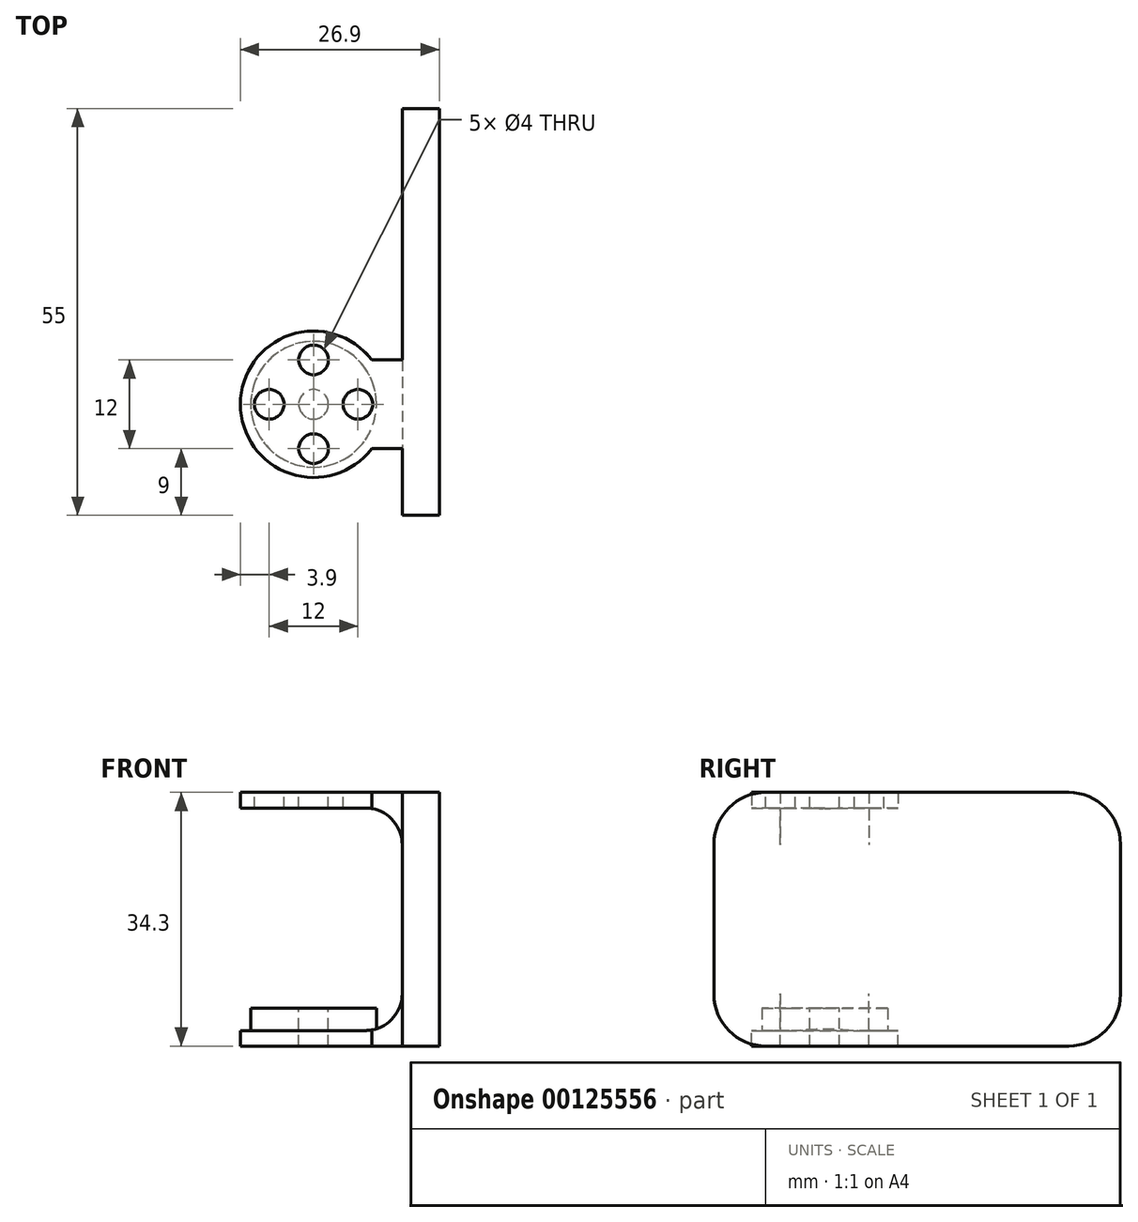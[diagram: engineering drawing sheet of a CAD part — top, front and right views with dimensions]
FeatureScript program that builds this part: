
annotation { "Feature Type Name" : "Feature", "Feature Type Description" : "" }
export const myFeature = defineFeature(function(context is Context, id is Id, definition is map)
    precondition{}
    {
        {
            var Q0;
            Q0=qCreatedBy(makeId("Top.planeOp"),FACE);
            var sketch = newSketch(context, id + "F0", { "sketchPlane" : qUnion([Q0])});
            skArc(sketch, "E0", {"start": v(7.87, 6) * mm, "mid": v(-9.9, 0) * mm, "end": v(7.87, -6) * mm});
            skLineSegment(sketch, "E1", {"start": v(7.87, 6) * mm, "end": v(12, 6) * mm});
            skLineSegment(sketch, "E2", {"start": v(12, 6) * mm, "end": v(12, 40) * mm});
            skLineSegment(sketch, "E3", {"start": v(12, 40) * mm, "end": v(17, 40) * mm});
            skLineSegment(sketch, "E4", {"start": v(17, 40) * mm, "end": v(17, -15) * mm});
            skLineSegment(sketch, "E5", {"start": v(17, -15) * mm, "end": v(12, -15) * mm});
            skLineSegment(sketch, "E6", {"start": v(12, -15) * mm, "end": v(12, -6) * mm});
            skLineSegment(sketch, "E7", {"start": v(12, -6) * mm, "end": v(7.87, -6) * mm});
            skSolve(sketch);
        }
        {
            var Q0;
            Q0=qSketchRegion(id+"F0",true);
            extrude(context, id + "F1", {"entities" : qUnion([Q0]), "depth" : 17.15 * mm});
        }
        {
            var Q0;
            Q0=qCreatedBy(makeId("Front.planeOp"),FACE);
            var sketch = newSketch(context, id + "F2", { "sketchPlane" : qUnion([Q0])});
            skLineSegment(sketch, "E8.bottom", {"start": v(-20, 15.05) * mm, "end": v(7, 15.05) * mm});
            skLineSegment(sketch, "E8.top", {"start": v(-20, 0) * mm, "end": v(12, 0) * mm});
            skLineSegment(sketch, "E8.left", {"start": v(-20, 15.05) * mm, "end": v(-20, 0) * mm});
            skLineSegment(sketch, "E8.right", {"start": v(12, 10.05) * mm, "end": v(12, 0) * mm});
            skPoint(sketch, "E9.visualSharp", {"position": v(12, 15.05) * mm});
            skArc(sketch, "E9.filletArc", {"start": v(12, 10.05) * mm, "mid": v(10.54, 13.59) * mm, "end": v(7, 15.05) * mm});
            skSolve(sketch);
        }
        {
            var Q0;
            Q0=qSketchRegion(id+"F2",true);
            extrude(context, id + "F3", {"entities" : qUnion([Q0]), "operationType" : NewBodyOperationType.REMOVE, "endBound" : BoundingType.THROUGH_ALL, "oppositeDirection" : true, "depth" : 25 * mm, "hasSecondDirection" : true, "secondDirectionBound" : BoundingType.THROUGH_ALL, "secondDirectionOppositeDirection" : false, "secondDirectionDepth" : 25 * mm});
        }
        {
            var Q0;
            Q0=makeQuery(id+"F1.opExtrude","SWEPT_BODY",BODY,{"disambiguationData":[OSD([sQuery(id+"F0.wireOp",EDGE,"E0"),sQuery(id+"F0.wireOp",EDGE,"6P5EcGxq-JUqI-CBL5-0zC6-SwB43NatiXiN"),sQuery(id+"F0.wireOp",EDGE,"WmPqxOhL-y9bk-pV19-5UxV-K0lxU9I4QW50"),sQuery(id+"F0.wireOp",EDGE,"Di974qKV-glCy-LQtE-R6xi-RdLjh6y6jq4b")])]});
            var Q1;
            Q1=qCreatedBy(makeId("Top.planeOp"),FACE);
            mirror(context, id + "F4", {"operationType" : NewBodyOperationType.ADD, "entities" : qUnion([Q0]), "mirrorPlane" : qUnion([Q1])});
        }
        {
            var Q0;
            Q0=makeQuery(id+"F4.opPattern","COPY",FACE,{"derivedFrom":makeQuery(id+"F3.boolean.opBoolean","COPY",FACE,{"derivedFrom":makeQuery(id+"F3.opExtrude","SWEPT_FACE",FACE,{"disambiguationData":[OSD([sQuery(id+"F2.wireOp",EDGE,"E8.bottom")])]})}),"instanceName":"1"});
            var sketch = newSketch(context, id + "F5", { "sketchPlane" : qUnion([Q0])});
            skCircle(sketch, "E10", {"center": v(0, 0) * mm, "radius": 8.5 * mm});
            skSolve(sketch);
        }
        {
            var Q0;
            Q0=qSketchRegion(id+"F5",true);
            extrude(context, id + "F6", {"entities" : qUnion([Q0]), "operationType" : NewBodyOperationType.ADD, "depth" : 3 * mm});
        }
        {
            var Q0;
            Q0=makeQuery(id+"F6.opExtrude","CAP_FACE",FACE,{"disambiguationData":[OSD([sQuery(id+"F5.wireOp",EDGE,"E10")])],"isStart":false});
            var sketch = newSketch(context, id + "F7", { "sketchPlane" : qUnion([Q0])});
            skCircle(sketch, "E11", {"center": v(0, 0) * mm, "radius": 2 * mm});
            skSolve(sketch);
        }
        {
            var Q0;
            Q0=qSketchRegion(id+"F7",true);
            extrude(context, id + "F8", {"entities" : qUnion([Q0]), "operationType" : NewBodyOperationType.REMOVE, "endBound" : BoundingType.THROUGH_ALL, "oppositeDirection" : true, "depth" : 25 * mm});
        }
        {
            var Q0;
            Q0=makeQuery(id+"F1.opExtrude","CAP_FACE",FACE,{"disambiguationData":[OSD([sQuery(id+"F0.wireOp",EDGE,"E0"),sQuery(id+"F0.wireOp",EDGE,"6P5EcGxq-JUqI-CBL5-0zC6-SwB43NatiXiN"),sQuery(id+"F0.wireOp",EDGE,"WmPqxOhL-y9bk-pV19-5UxV-K0lxU9I4QW50"),sQuery(id+"F0.wireOp",EDGE,"Di974qKV-glCy-LQtE-R6xi-RdLjh6y6jq4b")])],"isStart":false});
            var sketch = newSketch(context, id + "F9", { "sketchPlane" : qUnion([Q0])});
            skCircle(sketch, "E12", {"center": v(6, 0) * mm, "radius": 2 * mm});
            skCircle(sketch, "E13", {"center": v(0, 0) * mm, "radius": 6 * mm, "construction": true});
            skCircle(sketch, "E14", {"center": v(0, -6) * mm, "radius": 2 * mm});
            skCircle(sketch, "E15", {"center": v(-6, 0) * mm, "radius": 2 * mm});
            skCircle(sketch, "E16", {"center": v(0, 6) * mm, "radius": 2 * mm});
            skSolve(sketch);
        }
        {
            var Q0;
            Q0=qSketchRegion(id+"F9",true);
            var Q1;
            Q1=qCreatedBy(makeId("Top.planeOp"),FACE);
            extrude(context, id + "F10", {"entities" : qUnion([Q0]), "operationType" : NewBodyOperationType.REMOVE, "endBound" : BoundingType.UP_TO_SURFACE, "oppositeDirection" : true, "endBoundEntityFace" : qUnion([Q1]), "depth" : 25 * mm});
        }
        {
            var Q0;
            Q0=makeQuery(id+"F1.opExtrude","CAP_EDGE",EDGE,{"disambiguationData":[OSD([sQuery(id+"F0.wireOp",EDGE,"E3")])],"isStart":false});
            var Q1;
            Q1=makeQuery(id+"F4.opPattern","COPY",EDGE,{"derivedFrom":makeQuery(id+"F1.opExtrude","CAP_EDGE",EDGE,{"disambiguationData":[OSD([sQuery(id+"F0.wireOp",EDGE,"E3")])],"isStart":false}),"instanceName":"1"});
            var Q2;
            Q2=makeQuery(id+"F4.opPattern","COPY",EDGE,{"derivedFrom":makeQuery(id+"F1.opExtrude","CAP_EDGE",EDGE,{"disambiguationData":[OSD([sQuery(id+"F0.wireOp",EDGE,"E5")])],"isStart":false}),"instanceName":"1"});
            var Q3;
            Q3=makeQuery(id+"F1.opExtrude","CAP_EDGE",EDGE,{"disambiguationData":[OSD([sQuery(id+"F0.wireOp",EDGE,"E5")])],"isStart":false});
            fillet(context, id + "F11", {"entities" : qUnion([Q0, Q1, Q2, Q3]), "radius" : 7 * mm, "tangentPropagation" : true, "allowEdgeOverflow" : false});
        }
    });
